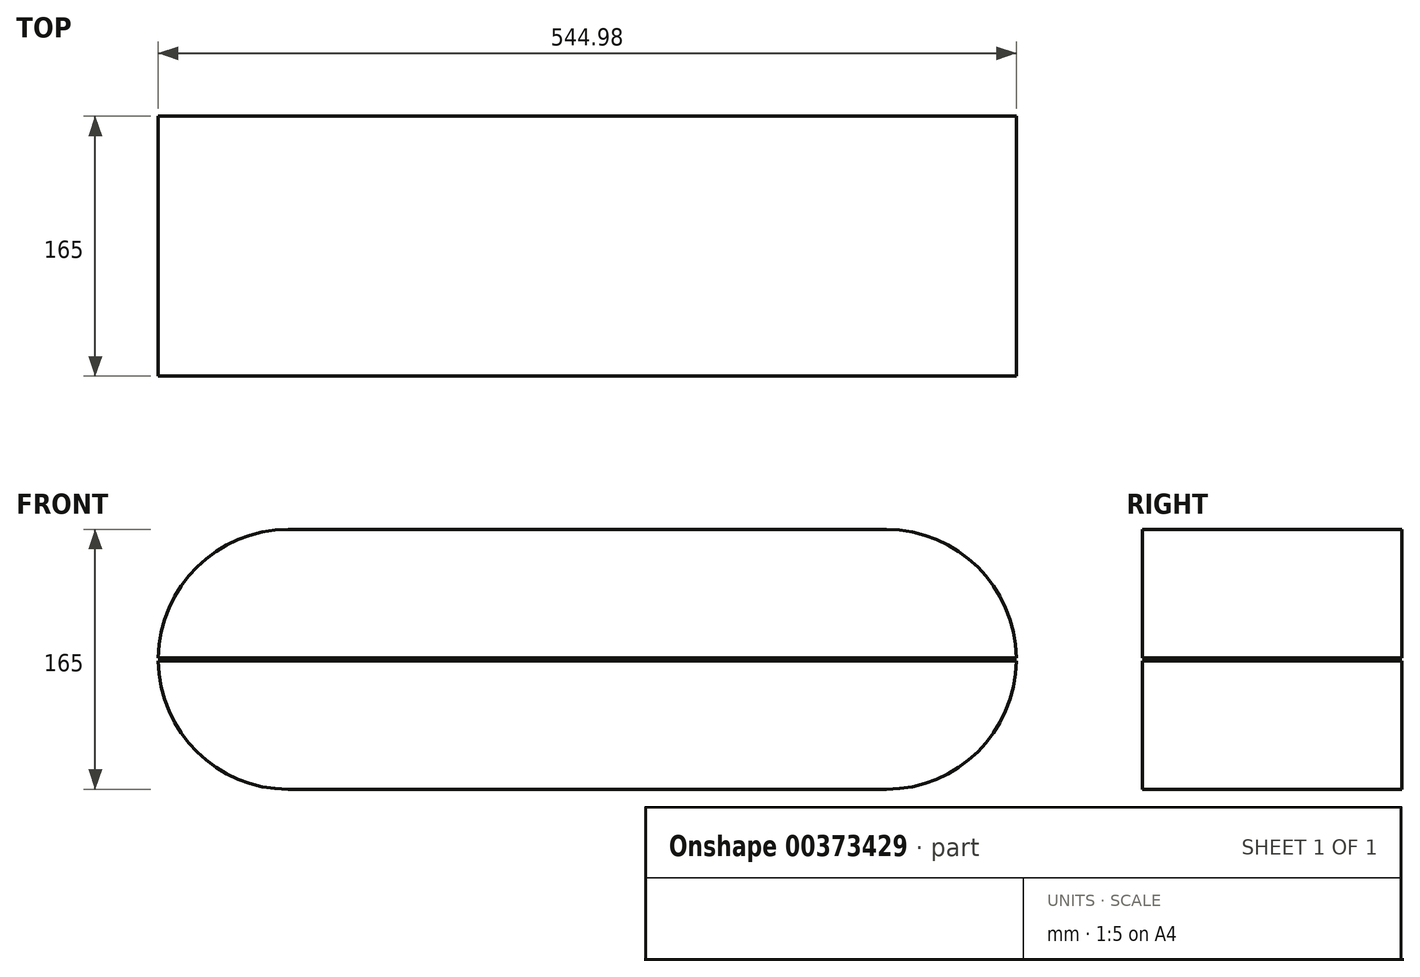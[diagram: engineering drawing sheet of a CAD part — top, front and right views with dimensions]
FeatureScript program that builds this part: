
annotation { "Feature Type Name" : "Feature", "Feature Type Description" : "" }
export const myFeature = defineFeature(function(context is Context, id is Id, definition is map)
    precondition{}
    {
        {
            var Q0;
            Q0=qCreatedBy(makeId("Front.planeOp"),FACE);
            var sketch = newSketch(context, id + "F0", { "sketchPlane" : qUnion([Q0])});
            skLineSegment(sketch, "E0.left", {"start": v(190, -1) * mm, "end": v(190, 1) * mm});
            skLineSegment(sketch, "E0.right", {"start": v(-190, -1) * mm, "end": v(-190, 1) * mm});
            skPoint(sketch, "E0.middle", {"position": v(0, 0) * mm});
            skArc(sketch, "E1", {"start": v(-190, 82.5) * mm, "mid": v(-272.5, 0) * mm, "end": v(-190, -82.5) * mm});
            skArc(sketch, "E2", {"start": v(190, -82.5) * mm, "mid": v(272.5, 0) * mm, "end": v(190, 82.5) * mm});
            skLineSegment(sketch, "E3", {"start": v(-272.5, 0) * mm, "end": v(272.5, 0) * mm, "construction": true});
            skLineSegment(sketch, "E4", {"start": v(190, -82.5) * mm, "end": v(-190, -82.5) * mm});
            skLineSegment(sketch, "E5", {"start": v(190, 82.5) * mm, "end": v(-190, 82.5) * mm});
            skLineSegment(sketch, "E6", {"start": v(-272.5, 1) * mm, "end": v(272.5, 1) * mm});
            skLineSegment(sketch, "E7", {"start": v(272.5, 0) * mm, "end": v(272.5, -1) * mm});
            skLineSegment(sketch, "E8", {"start": v(272.5, -1) * mm, "end": v(-272.5, -1) * mm});
            skSolve(sketch);
        }
        {
            var Q0;
            {var subQ4=sQuery(id+"F0.wireOp",EDGE,"E5");Q0=makeQuery(id+"F0.imprint","IMPRINT",FACE,{"disambiguationData":[TD([[makeQuery(id+"F0.imprint","IMPRINT",EDGE,{"derivedFrom":subQ4}),1.0]])]});}
            var Q1;
            {var subQ4=sQuery(id+"F0.wireOp",EDGE,"E4");Q1=makeQuery(id+"F0.imprint","IMPRINT",FACE,{"disambiguationData":[TD([[makeQuery(id+"F0.imprint","IMPRINT",EDGE,{"derivedFrom":subQ4}),-1.0]])]});}
            extrude(context, id + "F1", {"entities" : qUnion([Q0, Q1]), "depth" : 165 * mm});
        }
    });
